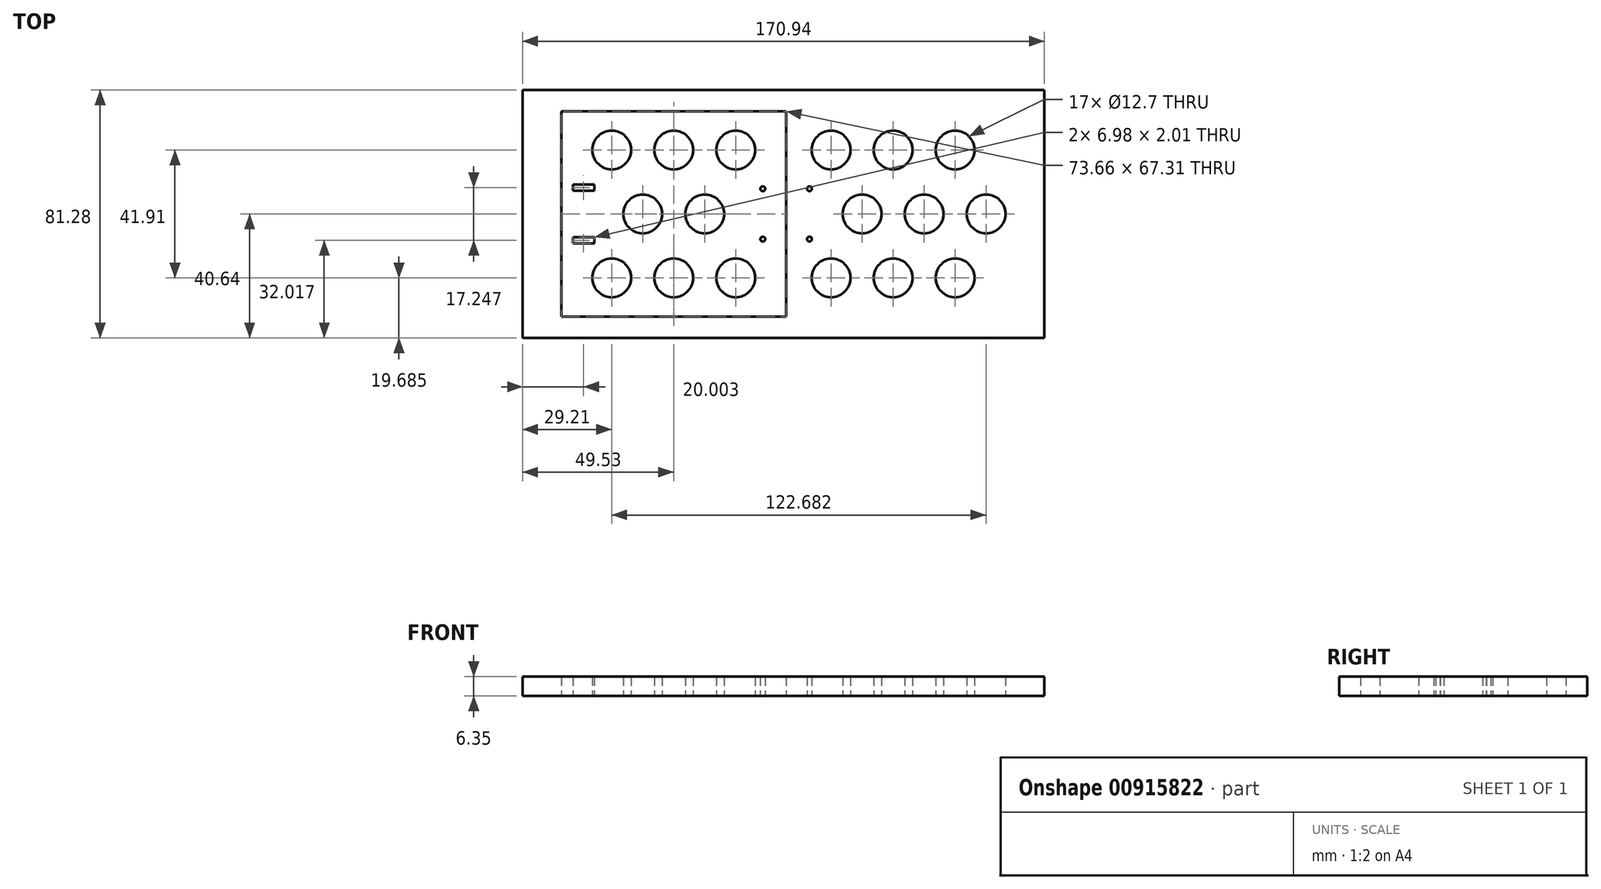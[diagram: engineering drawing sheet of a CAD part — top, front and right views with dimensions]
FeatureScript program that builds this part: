
annotation { "Feature Type Name" : "Feature", "Feature Type Description" : "" }
export const myFeature = defineFeature(function(context is Context, id is Id, definition is map)
    precondition{}
    {
        {
            var Q0;
            Q0=qCreatedBy(makeId("Top.planeOp"),FACE);
            var sketch = newSketch(context, id + "F0", { "sketchPlane" : qUnion([Q0])});
            skLineSegment(sketch, "E0.bottom", {"start": v(0, 0) * mm, "end": v(170.94, 0) * mm});
            skLineSegment(sketch, "E0.top", {"start": v(0, -81.28) * mm, "end": v(170.94, -81.28) * mm});
            skLineSegment(sketch, "E0.left", {"start": v(0, 0) * mm, "end": v(0, -81.28) * mm});
            skLineSegment(sketch, "E0.right", {"start": v(170.94, 0) * mm, "end": v(170.94, -81.28) * mm});
            skLineSegment(sketch, "E1.bottom", {"start": v(12.7, -6.99) * mm, "end": v(86.36, -6.99) * mm});
            skLineSegment(sketch, "E1.top", {"start": v(12.7, -74.3) * mm, "end": v(86.36, -74.3) * mm});
            skLineSegment(sketch, "E1.left", {"start": v(12.7, -6.99) * mm, "end": v(12.7, -74.3) * mm});
            skLineSegment(sketch, "E1.right", {"start": v(86.36, -6.99) * mm, "end": v(86.36, -74.3) * mm});
            skLineSegment(sketch, "E2", {"start": v(0, -40.64) * mm, "end": v(12.7, -40.64) * mm, "construction": true});
            skCircle(sketch, "E3", {"center": v(29.21, -19.69) * mm, "radius": 6.35 * mm});
            skCircle(sketch, "E4", {"center": v(49.53, -19.69) * mm, "radius": 6.35 * mm});
            skCircle(sketch, "E5", {"center": v(69.85, -19.69) * mm, "radius": 6.35 * mm});
            skLineSegment(sketch, "E6", {"start": v(12.7, -19.69) * mm, "end": v(29.21, -19.69) * mm, "construction": true});
            skLineSegment(sketch, "E7", {"start": v(49.53, -19.69) * mm, "end": v(29.21, -19.69) * mm, "construction": true});
            skLineSegment(sketch, "E8", {"start": v(49.53, -19.69) * mm, "end": v(69.85, -19.69) * mm, "construction": true});
            skLineSegment(sketch, "E9", {"start": v(49.53, -6.99) * mm, "end": v(49.53, -19.69) * mm, "construction": true});
            skCircle(sketch, "E10", {"center": v(39.37, -40.64) * mm, "radius": 6.35 * mm});
            skCircle(sketch, "E11", {"center": v(59.7, -40.64) * mm, "radius": 6.35 * mm});
            skLineSegment(sketch, "E12", {"start": v(12.7, -40.64) * mm, "end": v(39.37, -40.64) * mm, "construction": true});
            skLineSegment(sketch, "E13", {"start": v(39.37, -40.64) * mm, "end": v(59.7, -40.64) * mm, "construction": true});
            skCircle(sketch, "E14.MirrorC", {"center": v(29.21, -61.6) * mm, "radius": 6.35 * mm});
            skCircle(sketch, "E15.MirrorC", {"center": v(49.53, -61.6) * mm, "radius": 6.35 * mm});
            skCircle(sketch, "E16.MirrorC", {"center": v(69.85, -61.6) * mm, "radius": 6.35 * mm});
            skLineSegment(sketch, "E17", {"start": v(85.47, 0) * mm, "end": v(85.47, -4.18) * mm, "construction": true});
            skCircle(sketch, "E18.MirrorC", {"center": v(101.1, -19.69) * mm, "radius": 6.35 * mm});
            skCircle(sketch, "E19.MirrorC", {"center": v(121.41, -19.69) * mm, "radius": 6.35 * mm});
            skCircle(sketch, "E20.MirrorC", {"center": v(141.73, -19.69) * mm, "radius": 6.35 * mm});
            skCircle(sketch, "E21.MirrorC", {"center": v(131.57, -40.64) * mm, "radius": 6.35 * mm});
            skCircle(sketch, "E22.MirrorC", {"center": v(111.25, -40.64) * mm, "radius": 6.35 * mm});
            skCircle(sketch, "E23.MirrorC", {"center": v(101.1, -61.6) * mm, "radius": 6.35 * mm});
            skCircle(sketch, "E24.MirrorC", {"center": v(121.41, -61.6) * mm, "radius": 6.35 * mm});
            skCircle(sketch, "E25.MirrorC", {"center": v(141.73, -61.6) * mm, "radius": 6.35 * mm});
            skCircle(sketch, "E26", {"center": v(151.9, -40.64) * mm, "radius": 6.35 * mm});
            skPoint(sketch, "E26.centerSnap0", {"position": v(170.94, -40.64) * mm});
            skLineSegment(sketch, "E27.bottom", {"start": v(16.51, -31.01) * mm, "end": v(23.5, -31.01) * mm});
            skLineSegment(sketch, "E27.top", {"start": v(16.51, -33.02) * mm, "end": v(23.5, -33.02) * mm});
            skLineSegment(sketch, "E27.left", {"start": v(16.51, -31.01) * mm, "end": v(16.51, -33.02) * mm});
            skLineSegment(sketch, "E27.right", {"start": v(23.5, -31.01) * mm, "end": v(23.5, -33.02) * mm});
            skLineSegment(sketch, "E28.MirrorCS", {"start": v(16.51, -50.27) * mm, "end": v(23.5, -50.27) * mm});
            skLineSegment(sketch, "E29.MirrorCS", {"start": v(23.5, -50.27) * mm, "end": v(23.5, -48.26) * mm});
            skLineSegment(sketch, "E30.MirrorCS", {"start": v(16.51, -48.26) * mm, "end": v(23.5, -48.26) * mm});
            skLineSegment(sketch, "E31.MirrorCS", {"start": v(16.51, -50.27) * mm, "end": v(16.51, -48.26) * mm});
            skLineSegment(sketch, "E32", {"start": v(86.36, -40.64) * mm, "end": v(86.36, -32.39) * mm});
            skLineSegment(sketch, "E33", {"start": v(86.36, -40.64) * mm, "end": v(86.36, -48.9) * mm});
            skLineSegment(sketch, "E34", {"start": v(86.36, -32.39) * mm, "end": v(78.71, -32.39) * mm});
            skLineSegment(sketch, "E35", {"start": v(86.36, -48.9) * mm, "end": v(78.71, -48.9) * mm});
            skCircle(sketch, "E36", {"center": v(78.71, -48.9) * mm, "radius": 0.8 * mm});
            skCircle(sketch, "E37", {"center": v(78.71, -32.39) * mm, "radius": 0.8 * mm});
            skLineSegment(sketch, "E38", {"start": v(86.36, -32.39) * mm, "end": v(94, -32.39) * mm});
            skLineSegment(sketch, "E39", {"start": v(86.36, -48.9) * mm, "end": v(94, -48.9) * mm});
            skCircle(sketch, "E40", {"center": v(94, -32.39) * mm, "radius": 0.8 * mm});
            skCircle(sketch, "E41", {"center": v(94, -48.9) * mm, "radius": 0.8 * mm});
            skSolve(sketch);
        }
        {
            var Q0;
            Q0=makeQuery(id+"F0.imprint","IMPRINT",FACE,{"disambiguationData":[TD([[makeQuery(id+"F0.imprint","IMPRINT",EDGE,{"derivedFrom":sQuery(id+"F0.wireOp",EDGE,"E0.bottom")}),-1.0]])]});
            extrude(context, id + "F1", {"entities" : qUnion([Q0]), "depth" : 6.35 * mm, "offsetDistance" : 25.4 * mm});
        }
        {
            var Q0;
            Q0=makeQuery(id+"F0.imprint","IMPRINT",FACE,{"disambiguationData":[TD([[makeQuery(id+"F0.imprint","IMPRINT",EDGE,{"derivedFrom":sQuery(id+"F0.wireOp",EDGE,"E1.bottom")}),-1.0]])]});
            extrude(context, id + "F2", {"entities" : qUnion([Q0]), "depth" : 6.35 * mm, "offsetDistance" : 25.4 * mm});
        }
    });
